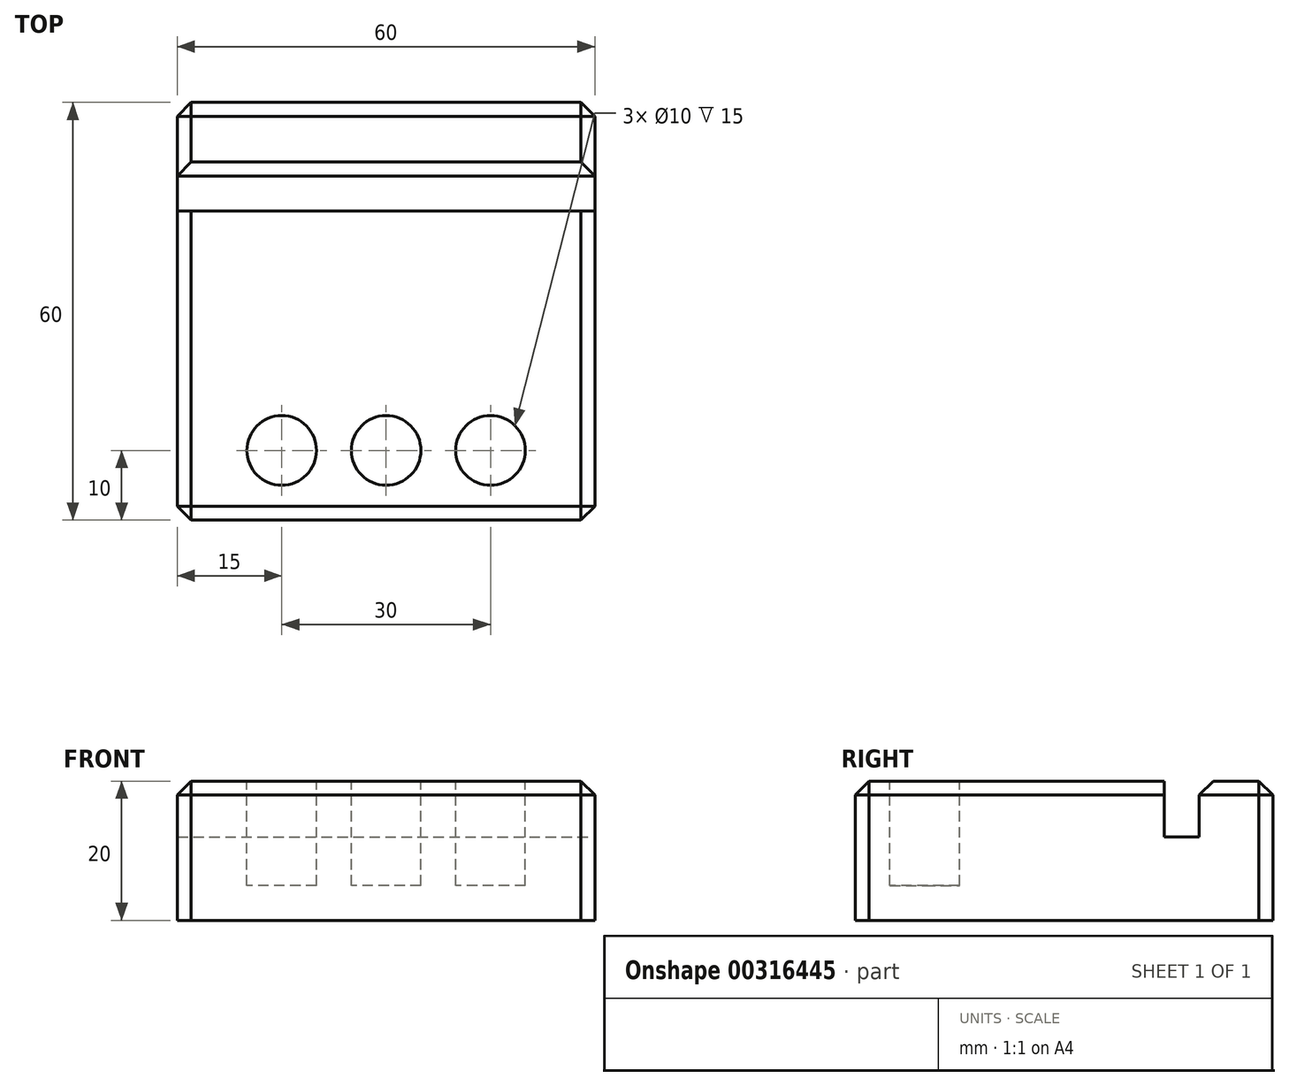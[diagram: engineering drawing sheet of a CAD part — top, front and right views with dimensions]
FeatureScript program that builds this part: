
annotation { "Feature Type Name" : "Feature", "Feature Type Description" : "" }
export const myFeature = defineFeature(function(context is Context, id is Id, definition is map)
    precondition{}
    {
        {
            var Q0;
            Q0=qCreatedBy(makeId("Top.planeOp"),FACE);
            var sketch = newSketch(context, id + "F0", { "sketchPlane" : qUnion([Q0])});
            skLineSegment(sketch, "E0.bottom", {"start": v(30, 30) * mm, "end": v(-30, 30) * mm});
            skLineSegment(sketch, "E0.top", {"start": v(30, -30) * mm, "end": v(-30, -30) * mm});
            skLineSegment(sketch, "E0.left", {"start": v(30, 30) * mm, "end": v(30, -30) * mm});
            skLineSegment(sketch, "E0.right", {"start": v(-30, 30) * mm, "end": v(-30, -30) * mm});
            skPoint(sketch, "E0.middle", {"position": v(0, 0) * mm});
            skSolve(sketch);
        }
        {
            var Q0;
            Q0=makeQuery(id+"F0.imprint","IMPRINT",FACE,{"disambiguationData":[TD([[makeQuery(id+"F0.imprint","IMPRINT",EDGE,{"derivedFrom":sQuery(id+"F0.wireOp",EDGE,"E0.bottom")}),1.0]])]});
            extrude(context, id + "F1", {"entities" : qUnion([Q0]), "depth" : 20 * mm});
        }
        {
            var Q0;
            Q0=makeQuery(id+"F1.opExtrude","CAP_FACE",FACE,{"disambiguationData":[OSD([sQuery(id+"F0.wireOp",EDGE,"E0.bottom"),sQuery(id+"F0.wireOp",EDGE,"E0.top"),sQuery(id+"F0.wireOp",EDGE,"E0.left"),sQuery(id+"F0.wireOp",EDGE,"E0.right")])],"isStart":false});
            var sketch = newSketch(context, id + "F2", { "sketchPlane" : qUnion([Q0])});
            skLineSegment(sketch, "E1.bottom", {"start": v(-30, 19.42) * mm, "end": v(30, 19.42) * mm});
            skLineSegment(sketch, "E1.top", {"start": v(-30, 14.42) * mm, "end": v(30, 14.42) * mm});
            skLineSegment(sketch, "E1.left", {"start": v(-30, 19.42) * mm, "end": v(-30, 14.42) * mm});
            skLineSegment(sketch, "E1.right", {"start": v(30, 19.42) * mm, "end": v(30, 14.42) * mm});
            skSolve(sketch);
        }
        {
            var Q0;
            Q0=makeQuery(id+"F2.imprint","IMPRINT",FACE,{"disambiguationData":[TD([[makeQuery(id+"F2.imprint","IMPRINT",EDGE,{"derivedFrom":sQuery(id+"F2.wireOp",EDGE,"E1.bottom")}),-1.0]])]});
            extrude(context, id + "F3", {"entities" : qUnion([Q0]), "operationType" : NewBodyOperationType.REMOVE, "oppositeDirection" : true, "depth" : 8 * mm});
        }
        {
            var Q0;
            {var subQ0=sQuery(id+"F0.wireOp",EDGE,"E0.top");var subQ1=sQuery(id+"F0.wireOp",EDGE,"E0.left");var subQ2=sQuery(id+"F0.wireOp",EDGE,"E0.right");Q0=makeQuery(id+"F3.boolean.opBoolean","SPLIT",FACE,{"disambiguationData":[TD([makeQuery(id+"F1.opExtrude","SWEPT_FACE",FACE,{"disambiguationData":[OSD([subQ0])]})])],"derivedFrom":makeQuery(id+"F1.opExtrude","CAP_FACE",FACE,{"disambiguationData":[OSD([sQuery(id+"F0.wireOp",EDGE,"E0.bottom"),subQ0,subQ1,subQ2])],"isStart":false})});}
            var sketch = newSketch(context, id + "F4", { "sketchPlane" : qUnion([Q0])});
            skCircle(sketch, "E2", {"center": v(-15, -20) * mm, "radius": 5 * mm});
            skCircle(sketch, "E3", {"center": v(0, -20) * mm, "radius": 5 * mm});
            skCircle(sketch, "E4", {"center": v(15, -20) * mm, "radius": 5 * mm});
            skSolve(sketch);
        }
        {
            var Q0;
            Q0=makeQuery(id+"F4.imprint","IMPRINT",FACE,{"disambiguationData":[TD([[makeQuery(id+"F4.imprint","IMPRINT",EDGE,{"derivedFrom":sQuery(id+"F4.wireOp",EDGE,"E3")}),1.0]])]});
            var Q1;
            Q1=makeQuery(id+"F4.imprint","IMPRINT",FACE,{"disambiguationData":[TD([[makeQuery(id+"F4.imprint","IMPRINT",EDGE,{"derivedFrom":sQuery(id+"F4.wireOp",EDGE,"E4")}),1.0]])]});
            var Q2;
            Q2=makeQuery(id+"F4.imprint","IMPRINT",FACE,{"disambiguationData":[TD([[makeQuery(id+"F4.imprint","IMPRINT",EDGE,{"derivedFrom":sQuery(id+"F4.wireOp",EDGE,"E2")}),1.0]])]});
            extrude(context, id + "F5", {"entities" : qUnion([Q0, Q1, Q2]), "operationType" : NewBodyOperationType.REMOVE, "oppositeDirection" : true, "depth" : 15 * mm});
        }
        {
            var Q0;
            Q0=makeQuery(id+"F1.opExtrude","CAP_EDGE",EDGE,{"disambiguationData":[OSD([sQuery(id+"F0.wireOp",EDGE,"E0.top")])],"isStart":false});
            var Q1;
            {var subQ0=sQuery(id+"F0.wireOp",EDGE,"E0.left");var subQ1=sQuery(id+"F0.wireOp",EDGE,"E0.top");Q1=makeQuery(id+"F3.boolean.opBoolean","SPLIT",EDGE,{"disambiguationData":[TD([makeQuery(id+"F1.opExtrude","SWEPT_FACE",FACE,{"disambiguationData":[OSD([subQ1])]})])],"derivedFrom":makeQuery(id+"F1.opExtrude","CAP_EDGE",EDGE,{"disambiguationData":[OSD([subQ0])],"isStart":false})});}
            var Q2;
            {var subQ0=sQuery(id+"F0.wireOp",EDGE,"E0.bottom");var subQ1=sQuery(id+"F0.wireOp",EDGE,"E0.left");Q2=makeQuery(id+"F3.boolean.opBoolean","SPLIT",EDGE,{"disambiguationData":[TD([makeQuery(id+"F1.opExtrude","SWEPT_FACE",FACE,{"disambiguationData":[OSD([subQ0])]})])],"derivedFrom":makeQuery(id+"F1.opExtrude","CAP_EDGE",EDGE,{"disambiguationData":[OSD([subQ1])],"isStart":false})});}
            var Q3;
            Q3=makeQuery(id+"F1.opExtrude","CAP_EDGE",EDGE,{"disambiguationData":[OSD([sQuery(id+"F0.wireOp",EDGE,"E0.bottom")])],"isStart":false});
            var Q4;
            {var subQ0=sQuery(id+"F0.wireOp",EDGE,"E0.right");var subQ1=sQuery(id+"F0.wireOp",EDGE,"E0.top");Q4=makeQuery(id+"F3.boolean.opBoolean","SPLIT",EDGE,{"disambiguationData":[TD([makeQuery(id+"F1.opExtrude","SWEPT_FACE",FACE,{"disambiguationData":[OSD([subQ1])]})])],"derivedFrom":makeQuery(id+"F1.opExtrude","CAP_EDGE",EDGE,{"disambiguationData":[OSD([subQ0])],"isStart":false})});}
            var Q5;
            {var subQ0=sQuery(id+"F0.wireOp",EDGE,"E0.bottom");var subQ1=sQuery(id+"F0.wireOp",EDGE,"E0.right");Q5=makeQuery(id+"F3.boolean.opBoolean","SPLIT",EDGE,{"disambiguationData":[TD([makeQuery(id+"F1.opExtrude","SWEPT_FACE",FACE,{"disambiguationData":[OSD([subQ0])]})])],"derivedFrom":makeQuery(id+"F1.opExtrude","CAP_EDGE",EDGE,{"disambiguationData":[OSD([subQ1])],"isStart":false})});}
            var Q6;
            Q6=makeQuery(id+"F5.boolean.opBoolean","COPY",EDGE,{"derivedFrom":makeQuery(id+"F5.opExtrude","CAP_EDGE",EDGE,{"disambiguationData":[OSD([sQuery(id+"F4.wireOp",EDGE,"E4")])],"isStart":true})});
            var Q7;
            Q7=makeQuery(id+"F5.boolean.opBoolean","COPY",EDGE,{"derivedFrom":makeQuery(id+"F5.opExtrude","CAP_EDGE",EDGE,{"disambiguationData":[OSD([sQuery(id+"F4.wireOp",EDGE,"E3")])],"isStart":true})});
            var Q8;
            Q8=makeQuery(id+"F5.boolean.opBoolean","COPY",EDGE,{"derivedFrom":makeQuery(id+"F5.opExtrude","CAP_EDGE",EDGE,{"disambiguationData":[OSD([sQuery(id+"F4.wireOp",EDGE,"E2")])],"isStart":true})});
            var Q9;
            Q9=makeQuery(id+"F3.boolean.opBoolean","COPY",EDGE,{"derivedFrom":makeQuery(id+"F3.opExtrude","CAP_EDGE",EDGE,{"disambiguationData":[OSD([sQuery(id+"F2.wireOp",EDGE,"E1.bottom")])],"isStart":true})});
            var Q10;
            Q10=makeQuery(id+"F3.boolean.opBoolean","COPY",EDGE,{"derivedFrom":makeQuery(id+"F3.opExtrude","CAP_EDGE",EDGE,{"disambiguationData":[OSD([sQuery(id+"F2.wireOp",EDGE,"E1.top")])],"isStart":true})});
            var Q11;
            Q11=makeQuery(id+"F1.opExtrude","SWEPT_EDGE",EDGE,{"disambiguationData":[OSD([sQuery(id+"F0.wireOp",EDGE,"E0.top"),sQuery(id+"F0.wireOp",EDGE,"E0.left")])]});
            var Q12;
            Q12=makeQuery(id+"F1.opExtrude","SWEPT_EDGE",EDGE,{"disambiguationData":[OSD([sQuery(id+"F0.wireOp",EDGE,"E0.top"),sQuery(id+"F0.wireOp",EDGE,"E0.right")])]});
            var Q13;
            Q13=makeQuery(id+"F1.opExtrude","SWEPT_EDGE",EDGE,{"disambiguationData":[OSD([sQuery(id+"F0.wireOp",EDGE,"E0.bottom"),sQuery(id+"F0.wireOp",EDGE,"E0.right")])]});
            var Q14;
            Q14=makeQuery(id+"F1.opExtrude","SWEPT_EDGE",EDGE,{"disambiguationData":[OSD([sQuery(id+"F0.wireOp",EDGE,"E0.bottom"),sQuery(id+"F0.wireOp",EDGE,"E0.left")])]});
            chamfer(context, id + "F6", {"entities" : qUnion([Q0, Q1, Q2, Q3, Q4, Q5, Q6, Q7, Q8, Q9, Q10, Q11, Q12, Q13, Q14]), "width" : 2 * mm, "tangentPropagation" : true});
        }
    });
